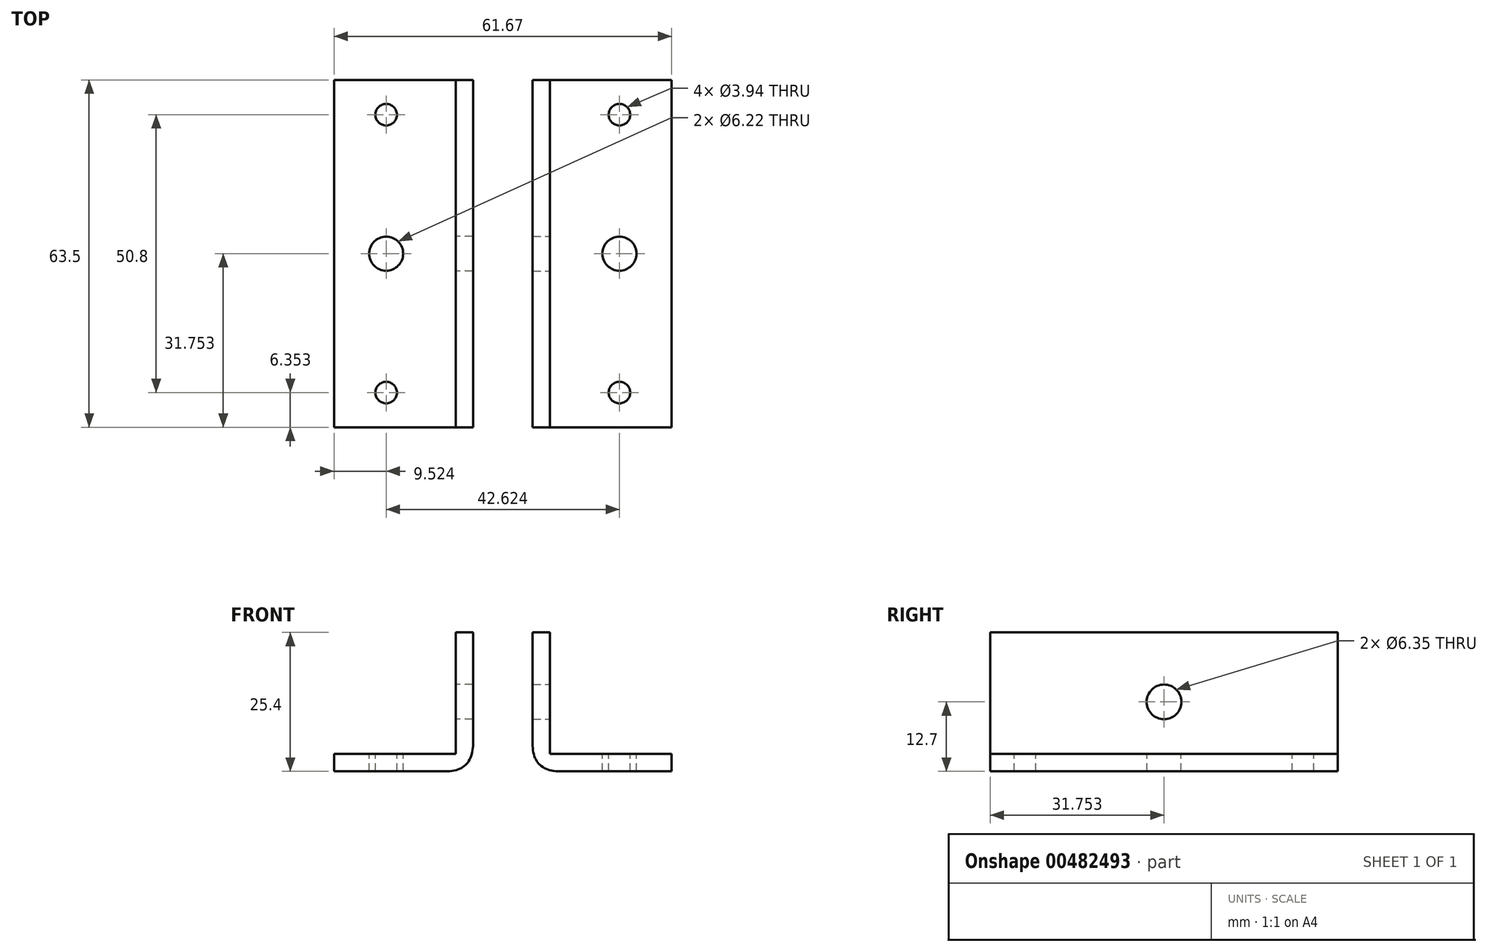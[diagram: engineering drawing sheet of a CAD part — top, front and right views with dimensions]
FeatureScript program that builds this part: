
annotation { "Feature Type Name" : "Feature", "Feature Type Description" : "" }
export const myFeature = defineFeature(function(context is Context, id is Id, definition is map)
    precondition{}
    {
        {
            var Q0;
            Q0=qCreatedBy(makeId("Top.planeOp"),FACE);
            var sketch = newSketch(context, id + "F0", { "sketchPlane" : qUnion([Q0])});
            skLineSegment(sketch, "E0.bottom", {"start": v(-41.84, 27.27) * mm, "end": v(-16.44, 27.27) * mm});
            skLineSegment(sketch, "E0.top", {"start": v(-41.84, -36.23) * mm, "end": v(-16.44, -36.23) * mm});
            skLineSegment(sketch, "E0.left", {"start": v(-41.84, 27.27) * mm, "end": v(-41.84, -36.23) * mm});
            skLineSegment(sketch, "E0.right", {"start": v(-16.44, 27.27) * mm, "end": v(-16.44, -36.23) * mm});
            skSolve(sketch);
        }
        {
            var Q0;
            Q0=makeQuery(id+"F0.imprint","IMPRINT",FACE,{"disambiguationData":[TD([[makeQuery(id+"F0.imprint","IMPRINT",EDGE,{"derivedFrom":sQuery(id+"F0.wireOp",EDGE,"E0.bottom")}),-1.0]])]});
            extrude(context, id + "F1", {"entities" : qUnion([Q0]), "depth" : 3.17 * mm});
        }
        {
            var Q0;
            Q0=makeQuery(id+"F1.opExtrude","CAP_FACE",FACE,{"disambiguationData":[OSD([sQuery(id+"F0.wireOp",EDGE,"E0.bottom"),sQuery(id+"F0.wireOp",EDGE,"E0.top"),sQuery(id+"F0.wireOp",EDGE,"E0.left"),sQuery(id+"F0.wireOp",EDGE,"E0.right")])],"isStart":false});
            var sketch = newSketch(context, id + "F2", { "sketchPlane" : qUnion([Q0])});
            skLineSegment(sketch, "E1.bottom", {"start": v(-16.44, 27.27) * mm, "end": v(-19.62, 27.27) * mm});
            skLineSegment(sketch, "E1.top", {"start": v(-16.44, -36.23) * mm, "end": v(-19.62, -36.23) * mm});
            skLineSegment(sketch, "E1.left", {"start": v(-16.44, 27.27) * mm, "end": v(-16.44, -36.23) * mm});
            skLineSegment(sketch, "E1.right", {"start": v(-19.62, 27.27) * mm, "end": v(-19.62, -36.23) * mm});
            skSolve(sketch);
        }
        {
            var Q0;
            Q0=makeQuery(id+"F2.imprint","IMPRINT",FACE,{"disambiguationData":[TD([[makeQuery(id+"F2.imprint","IMPRINT",EDGE,{"derivedFrom":sQuery(id+"F2.wireOp",EDGE,"E1.bottom")}),-1.0]])]});
            extrude(context, id + "F3", {"entities" : qUnion([Q0]), "operationType" : NewBodyOperationType.ADD, "depth" : 22.22 * mm});
        }
        {
            var Q0;
            Q0=makeQuery(id+"F3.opExtrude","SWEPT_FACE",FACE,{"disambiguationData":[OSD([sQuery(id+"F2.wireOp",EDGE,"E1.right")])]});
            var sketch = newSketch(context, id + "F4", { "sketchPlane" : qUnion([Q0])});
            skCircle(sketch, "E2", {"center": v(4.48, 12.7) * mm, "radius": 3.18 * mm});
            skSolve(sketch);
        }
        {
            var Q0;
            Q0=makeQuery(id+"F4.imprint","IMPRINT",FACE,{"disambiguationData":[TD([[makeQuery(id+"F4.imprint","IMPRINT",EDGE,{"derivedFrom":sQuery(id+"F4.wireOp",EDGE,"E2")}),1.0]])]});
            extrude(context, id + "F5", {"entities" : qUnion([Q0]), "operationType" : NewBodyOperationType.REMOVE, "oppositeDirection" : true, "depth" : 3.17 * mm});
        }
        {
            var Q0;
            Q0=makeQuery(id+"F1.opExtrude","CAP_FACE",FACE,{"disambiguationData":[OSD([sQuery(id+"F0.wireOp",EDGE,"E0.bottom"),sQuery(id+"F0.wireOp",EDGE,"E0.top"),sQuery(id+"F0.wireOp",EDGE,"E0.left"),sQuery(id+"F0.wireOp",EDGE,"E0.right")])],"isStart":false});
            var sketch = newSketch(context, id + "F6", { "sketchPlane" : qUnion([Q0])});
            skCircle(sketch, "E3", {"center": v(-32.32, 20.92) * mm, "radius": 1.97 * mm});
            skSolve(sketch);
        }
        {
            var Q0;
            Q0=makeQuery(id+"F6.imprint","IMPRINT",FACE,{"disambiguationData":[TD([[makeQuery(id+"F6.imprint","IMPRINT",EDGE,{"derivedFrom":sQuery(id+"F6.wireOp",EDGE,"E3")}),1.0]])]});
            extrude(context, id + "F7", {"entities" : qUnion([Q0]), "operationType" : NewBodyOperationType.REMOVE, "oppositeDirection" : true, "depth" : 3.17 * mm});
        }
        {
            var Q0;
            Q0=makeQuery(id+"F1.opExtrude","CAP_FACE",FACE,{"disambiguationData":[OSD([sQuery(id+"F0.wireOp",EDGE,"E0.bottom"),sQuery(id+"F0.wireOp",EDGE,"E0.top"),sQuery(id+"F0.wireOp",EDGE,"E0.left"),sQuery(id+"F0.wireOp",EDGE,"E0.right")])],"isStart":false});
            var sketch = newSketch(context, id + "F8", { "sketchPlane" : qUnion([Q0])});
            skCircle(sketch, "E4", {"center": v(-32.32, -29.88) * mm, "radius": 1.97 * mm});
            skSolve(sketch);
        }
        {
            var Q0;
            Q0=makeQuery(id+"F8.imprint","IMPRINT",FACE,{"disambiguationData":[TD([[makeQuery(id+"F8.imprint","IMPRINT",EDGE,{"derivedFrom":sQuery(id+"F8.wireOp",EDGE,"E4")}),1.0]])]});
            extrude(context, id + "F9", {"entities" : qUnion([Q0]), "operationType" : NewBodyOperationType.REMOVE, "oppositeDirection" : true, "depth" : 3.17 * mm});
        }
        {
            var Q0;
            Q0=makeQuery(id+"F1.opExtrude","CAP_FACE",FACE,{"disambiguationData":[OSD([sQuery(id+"F0.wireOp",EDGE,"E0.bottom"),sQuery(id+"F0.wireOp",EDGE,"E0.top"),sQuery(id+"F0.wireOp",EDGE,"E0.left"),sQuery(id+"F0.wireOp",EDGE,"E0.right")])],"isStart":false});
            var sketch = newSketch(context, id + "F10", { "sketchPlane" : qUnion([Q0])});
            skCircle(sketch, "E5", {"center": v(-32.32, -4.48) * mm, "radius": 3.11 * mm});
            skSolve(sketch);
        }
        {
            var Q0;
            Q0=makeQuery(id+"F10.imprint","IMPRINT",FACE,{"disambiguationData":[TD([[makeQuery(id+"F10.imprint","IMPRINT",EDGE,{"derivedFrom":sQuery(id+"F10.wireOp",EDGE,"E5")}),1.0]])]});
            extrude(context, id + "F11", {"entities" : qUnion([Q0]), "operationType" : NewBodyOperationType.REMOVE, "oppositeDirection" : true, "depth" : 3.17 * mm});
        }
        {
            var Q0;
            Q0=qCreatedBy(makeId("Top.planeOp"),FACE);
            var sketch = newSketch(context, id + "F12", { "sketchPlane" : qUnion([Q0])});
            skLineSegment(sketch, "E6.bottom", {"start": v(-5.57, 27.27) * mm, "end": v(19.83, 27.27) * mm});
            skLineSegment(sketch, "E6.top", {"start": v(-5.57, -36.23) * mm, "end": v(19.83, -36.23) * mm});
            skLineSegment(sketch, "E6.left", {"start": v(-5.57, 27.27) * mm, "end": v(-5.57, -36.23) * mm});
            skLineSegment(sketch, "E6.right", {"start": v(19.83, 27.27) * mm, "end": v(19.83, -36.23) * mm});
            skSolve(sketch);
        }
        {
            var Q0;
            Q0=makeQuery(id+"F12.imprint","IMPRINT",FACE,{"disambiguationData":[TD([[makeQuery(id+"F12.imprint","IMPRINT",EDGE,{"derivedFrom":sQuery(id+"F12.wireOp",EDGE,"E6.bottom")}),-1.0]])]});
            extrude(context, id + "F13", {"entities" : qUnion([Q0]), "depth" : 3.17 * mm, "offsetDistance" : 25.4 * mm});
        }
        {
            var Q0;
            Q0=makeQuery(id+"F13.opExtrude","CAP_FACE",FACE,{"disambiguationData":[OSD([sQuery(id+"F12.wireOp",EDGE,"E6.bottom"),sQuery(id+"F12.wireOp",EDGE,"E6.top"),sQuery(id+"F12.wireOp",EDGE,"E6.left"),sQuery(id+"F12.wireOp",EDGE,"E6.right")])],"isStart":false});
            var sketch = newSketch(context, id + "F14", { "sketchPlane" : qUnion([Q0])});
            skCircle(sketch, "E7", {"center": v(10.3, -4.48) * mm, "radius": 3.11 * mm});
            skPoint(sketch, "E7.centerSnap0", {"position": v(-5.57, -4.48) * mm});
            skSolve(sketch);
        }
        {
            var Q0;
            Q0=makeQuery(id+"F14.imprint","IMPRINT",FACE,{"disambiguationData":[TD([[makeQuery(id+"F14.imprint","IMPRINT",EDGE,{"derivedFrom":sQuery(id+"F14.wireOp",EDGE,"E7")}),-1.0]])]});
            var sketch = newSketch(context, id + "F15", { "sketchPlane" : qUnion([Q0])});
            skCircle(sketch, "E8", {"center": v(10.3, 20.92) * mm, "radius": 1.97 * mm});
            skCircle(sketch, "E9", {"center": v(10.3, -29.88) * mm, "radius": 1.97 * mm});
            skSolve(sketch);
        }
        {
            var Q0;
            Q0=makeQuery(id+"F14.imprint","IMPRINT",FACE,{"disambiguationData":[TD([[makeQuery(id+"F14.imprint","IMPRINT",EDGE,{"derivedFrom":sQuery(id+"F14.wireOp",EDGE,"E7")}),1.0]])]});
            var Q1;
            Q1 = qSketchRegion(id + "F15", true);
            extrude(context, id + "F16", {"entities" : qUnion([Q0, Q1]), "operationType" : NewBodyOperationType.REMOVE, "oppositeDirection" : true, "depth" : 3.17 * mm, "offsetDistance" : 25.4 * mm});
        }
        {
            var Q0;
            Q0=makeQuery(id+"F13.opExtrude","CAP_FACE",FACE,{"disambiguationData":[OSD([sQuery(id+"F12.wireOp",EDGE,"E6.bottom"),sQuery(id+"F12.wireOp",EDGE,"E6.top"),sQuery(id+"F12.wireOp",EDGE,"E6.left"),sQuery(id+"F12.wireOp",EDGE,"E6.right")])],"isStart":false});
            var sketch = newSketch(context, id + "F17", { "sketchPlane" : qUnion([Q0])});
            skLineSegment(sketch, "E10.bottom", {"start": v(-5.57, 27.27) * mm, "end": v(-2.4, 27.27) * mm});
            skLineSegment(sketch, "E10.top", {"start": v(-5.57, -36.23) * mm, "end": v(-2.4, -36.23) * mm});
            skLineSegment(sketch, "E10.left", {"start": v(-5.57, 27.27) * mm, "end": v(-5.57, -36.23) * mm});
            skLineSegment(sketch, "E10.right", {"start": v(-2.4, 27.27) * mm, "end": v(-2.4, -36.23) * mm});
            skSolve(sketch);
        }
        {
            var Q0;
            Q0=makeQuery(id+"F17.imprint","IMPRINT",FACE,{"disambiguationData":[TD([[makeQuery(id+"F17.imprint","IMPRINT",EDGE,{"derivedFrom":sQuery(id+"F17.wireOp",EDGE,"E10.bottom")}),-1.0]])]});
            extrude(context, id + "F18", {"entities" : qUnion([Q0]), "operationType" : NewBodyOperationType.ADD, "depth" : 22.22 * mm, "offsetDistance" : 25.4 * mm});
        }
        {
            var Q0;
            Q0=makeQuery(id+"F18.opExtrude","SWEPT_FACE",FACE,{"disambiguationData":[OSD([sQuery(id+"F17.wireOp",EDGE,"E10.right")])]});
            var sketch = newSketch(context, id + "F19", { "sketchPlane" : qUnion([Q0])});
            skCircle(sketch, "E11", {"center": v(-4.48, 12.7) * mm, "radius": 3.18 * mm});
            skPoint(sketch, "E11.centerSnap0", {"position": v(-4.48, 25.4) * mm});
            skSolve(sketch);
        }
        {
            var Q0;
            Q0=makeQuery(id+"F19.imprint","IMPRINT",FACE,{"disambiguationData":[TD([[makeQuery(id+"F19.imprint","IMPRINT",EDGE,{"derivedFrom":sQuery(id+"F19.wireOp",EDGE,"E11")}),1.0]])]});
            extrude(context, id + "F20", {"entities" : qUnion([Q0]), "operationType" : NewBodyOperationType.REMOVE, "oppositeDirection" : true, "depth" : 3.17 * mm, "offsetDistance" : 25.4 * mm});
        }
        {
            var Q0;
            Q0=makeQuery(id+"F3.opExtrude","CAP_EDGE",EDGE,{"disambiguationData":[OSD([sQuery(id+"F2.wireOp",EDGE,"E1.right")])],"isStart":true});
            var Q1;
            Q1=makeQuery(id+"F18.opExtrude","CAP_EDGE",EDGE,{"disambiguationData":[OSD([sQuery(id+"F17.wireOp",EDGE,"E10.right")])],"isStart":true});
            var Q2;
            Q2=makeQuery(id+"F13.opExtrude","CAP_EDGE",EDGE,{"disambiguationData":[OSD([sQuery(id+"F12.wireOp",EDGE,"E6.left")])],"isStart":true});
            var Q3;
            Q3=makeQuery(id+"F1.opExtrude","CAP_EDGE",EDGE,{"disambiguationData":[OSD([sQuery(id+"F0.wireOp",EDGE,"E0.right")])],"isStart":true});
            fillet(context, id + "F21", {"entities" : qUnion([Q0, Q1, Q2, Q3]), "radius" : 5.08 * mm, "tangentPropagation" : true, "rho" : 0.5, "crossSection" : FilletCrossSection.CONIC, "allowEdgeOverflow" : false});
        }
    });
